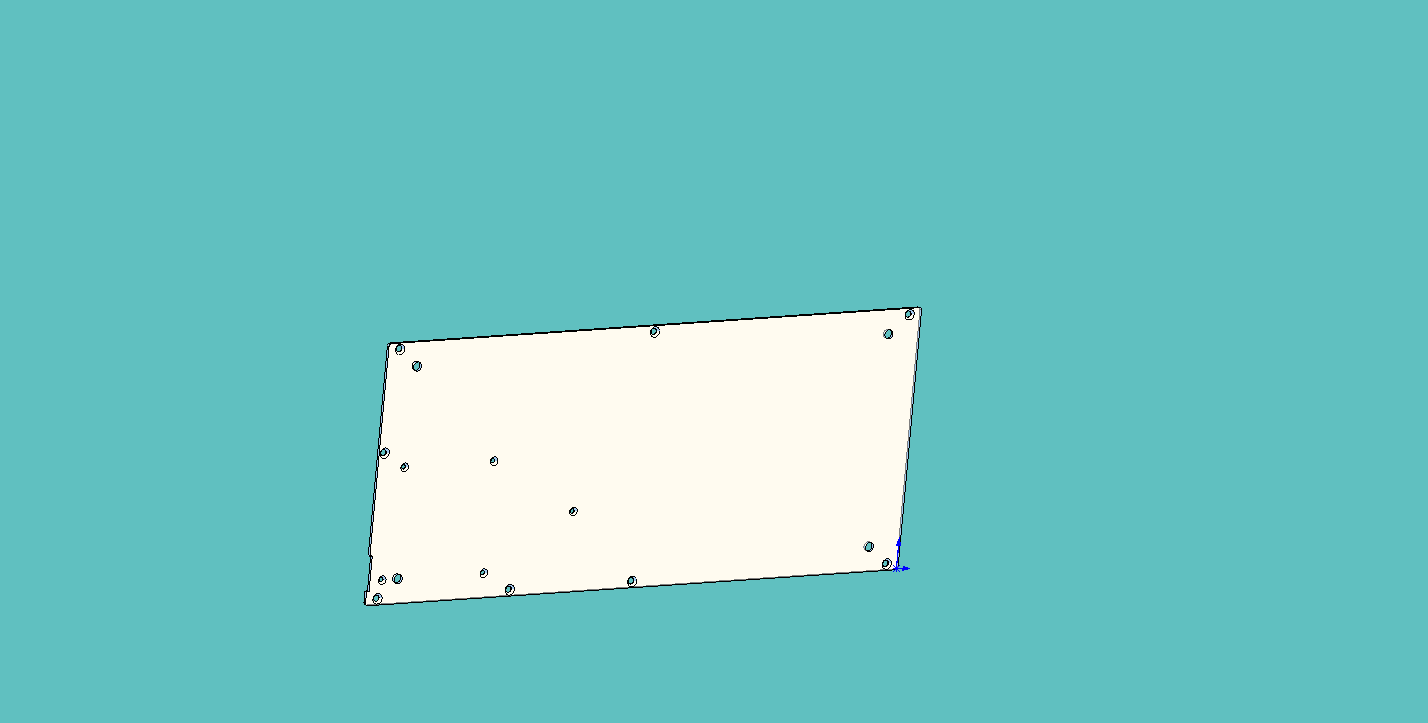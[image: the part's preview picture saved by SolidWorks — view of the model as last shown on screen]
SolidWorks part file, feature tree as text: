
SOLIDWORKS PART (.sldprt)
format: sldprt  version: not decoded by parser v0  size: 290,304 bytes
history: native  units: mm
features: plane x3, chamfer x2, material x1, sketch x1, extrude x1, fillet x1 (+10 scaffold rows collapsed)
feature tree (19):
  scaffold x10  (default folders/planes/origin — collapsed)
  material  "PE haute densité"
  plane  "Plan de face"
  plane  "Plan de dessus"
  plane  "Plan de droite"
  sketch  "Esquisse1"  dims[c1.D25=4.5mm c1.D26=4.5mm c1.D27=4.5mm c1.D28=6.5mm c1.D29=3.0mm c1.D30=3.2mm c1.D1=9.5mm c1.D2=185.0mm c1.D3=180.5mm c1.D4=167.5mm c1.D5=435.0mm c1.D6=4.5mm c1.D7=17.5mm c1.D8=2.0mm c1.D9=35.0mm c1.D10=25.0mm c1.D11=9.5mm c1.D12=117.5mm c1.D13=95.0mm c1.D14=22.0mm c1.D15=12.0mm c1.D16=25.0mm c1.D17=17.5mm c1.D18=96.5mm c1.D19=217.5mm c1.D20=217.5mm c1.D21=425.5mm c1.D22=425.5mm c1.D23=410.0mm c1.D24=25.0mm c2.D25=35.0mm c2.D26=4.5mm c2.D27=107.5mm c2.D30=164.0mm c2.D31=57.0mm]
  extrude  "Extrusion1"  Depth=2mm
  chamfer  "Chanfrein1"  Distance=1.5mm Angle=45deg
  chamfer  "Chanfrein2"  Distance=2mm Angle=45deg
  fillet  "Congé1"  Radius=2mm
decode coverage: 5 of 5 modeling features carry decoded parameters
note: suppression state not decoded; provenance and decode notes live in map.json
